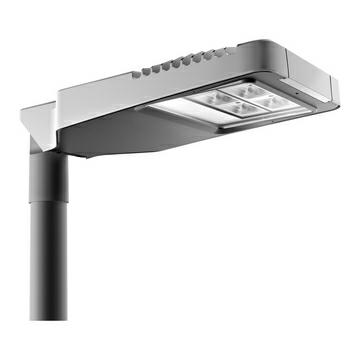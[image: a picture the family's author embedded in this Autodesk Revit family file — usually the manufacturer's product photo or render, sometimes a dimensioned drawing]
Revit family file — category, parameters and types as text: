
# Revit family: Lighting-Stradale-GEWISS-ROAD[5]MEDIUM-LED_OTTICA_WIDE-W_NEMA-ZAGA
name_source: partatom
category: Apparecchi per illuminazione
units: mm (PartAtom-declared; Revit-internal decimal feet)

## family parameters
Basato su piano di lavoro = No
Condiviso = No
Punto di calcolo locali = No
Quota connettore circolare = Usa diametro
Sempre verticale = Sì
Sorgente d'illuminazione = No
Taglio con vuoti quando caricato = No
Tipo di parte = Normale

## types (1)
- Lighting-Stradale-GEWISS-ROAD[5]MEDIUM-LED_OTTICA_WIDE-W_NEMA-ZAGA
    Alimentatore = Incluso
    Apparecchio a ridotta temperatura superficiale = -
    Applicazione = Esterno
    Cablaggio = Sezionatore
    Caratteristiche elettriche e gestione della luce = -
    Caratteristiche ottiche e illuminotecniche = -
    Catalogo = LIGHTING
    Catalogo Serie = ROAD [5]
    Certificazione DIN 18032-3 = -
    Certificazioni e classificazioni = -
    Classe fotobiologica = RG0
    Classe isolamento = II
    Classificazione: = -
    Codice Electrocod = 244C
    Codice digitale univoco (Datamatrix) = Attualmente non presente
    Colore = Grigio grafite
    Contesto = Illuminazione stradale e parcheggi
    Controllo abbagliamento e luminanza = G*4 - ULOR = 0
    Corpo = Alluminio pressofuso
    Corrente di pilotaggio. = 0,5A
    Descrizione = GWR5254ZW - ROAD5 MEDI WIDE 4M 4000K 0,50A CL2 W ZHA
    Dispositivo di protezione = DM 10KV / CM 10KV
    Distanza minima dall'oggetto illuminato = 1M
    Durata di vita = L90B10 (Tq+25°C) = 100.000 h
    Efficienza luminosa (lm/W) = 110
    Finitura colore = Verniciato a polveri
    Fissaggio = Testa palo - Sbraccio
    Frequenza nominale (Hz) = 50 / 60
    Gancio di chiusura = Maniglia frontale integrata
    Garanzia = 5 anni
    Grado di protezione = IP66
    Gruppo ottico = Riflettore in PC metallizzato
    Guarnizioni = silicone antinvecchiamento
    IDF = 1704a020-60df-4bb4-9be7-98e3354d3874
    IDT = d586ed85c3ba44b3a220029348af3ca9
    IPEA = STRADALE = A+ // GRANDI AREE = A4+ // CICLOPEDONALI = A+ // AREE VERDI = A+ // CENTRO STORICO = A5+
    Immagine tipo = GWR5276M.jpg
    Inclinazione = -20° ÷ +10° sbraccio - -10° ÷ +20° testa palo
    Indice di resa cromatica = CRI-70
    Informazioni generali = -
    Installazione e manutenzione = -
    LED Life time (L80B10) = 100000H
    Lampada = LED
    Lampada: = LED
    Lumen output (lm) = 16100
    Materiali = -
    Modello = GWR5254ZW
    Norma di riferimento = EN 60598-2-3, EN 60598-1 IEC/TR 62778
    Numero moduli = 4 (4x3 LED)
    Ottica = WIDE
    Peso (kg): = 8,4
    Potenza assorbita : = 146 W @ 0.5A
    Potenza di sistema = 146W
    Produttore = GEWISS S.p.A.
    Regolazione inclinazione = -20° ÷ +10° sbraccio - -10° ÷ +20° testa palo
    Resistenza agli urti = IK08
    Resistenza al filo incandescente = -
    Resistenza alle sovratensioni = 10 KV in modalità comune
    SEO = Stradale
    Scheda Tecnica = https://www.gewiss.com
    Schermo = Vetro piano temperato spessore 4mm
    Sistema di controllo = Telegestione con modulo Zhaga
    Sostituibilità gruppo ottico = Non disponibile
    Sostituibilità piastra di cablaggio = Non disponibile
    Superficie massima esposta al vento = 0,19M2
    Superficie massima esposta al vento : = 0.19 m2
    Temperatura di colore = 4000K
    Temperatura di colore: = 4000 K (CRI>70)
    Temperatura di esercizio = -25 +30 °C
    Temperatura di stoccaggio = -
    Temperatura di utilizzo = -25 +30 °C
    Tensione = 220 / 240 V - 50 / 60 Hz
    Tensione di alimentazione = 220 - 240 V
    Tipo alimentatore = Driver Led in corrente continua
    Tipo di apparecchio = Apparecchiatura stradale a LED
    Tipo di installazione e montaggio = Testa palo - Sbraccio
    Tipologia = Biregime
    Tipologia sorgente luminosa = LED - Non sostituibile
    Tolleranza cromatica = SDCM = 5
    URL = https://www.gewiss.com
    Vano di alimentazione = Integrato
    Versione file RFA = 20.11
    Viti esterne = Acciaio inox

## geometry (parser evidence)
native form markers: Blend x2
no freeform markers — native parametric forms only
